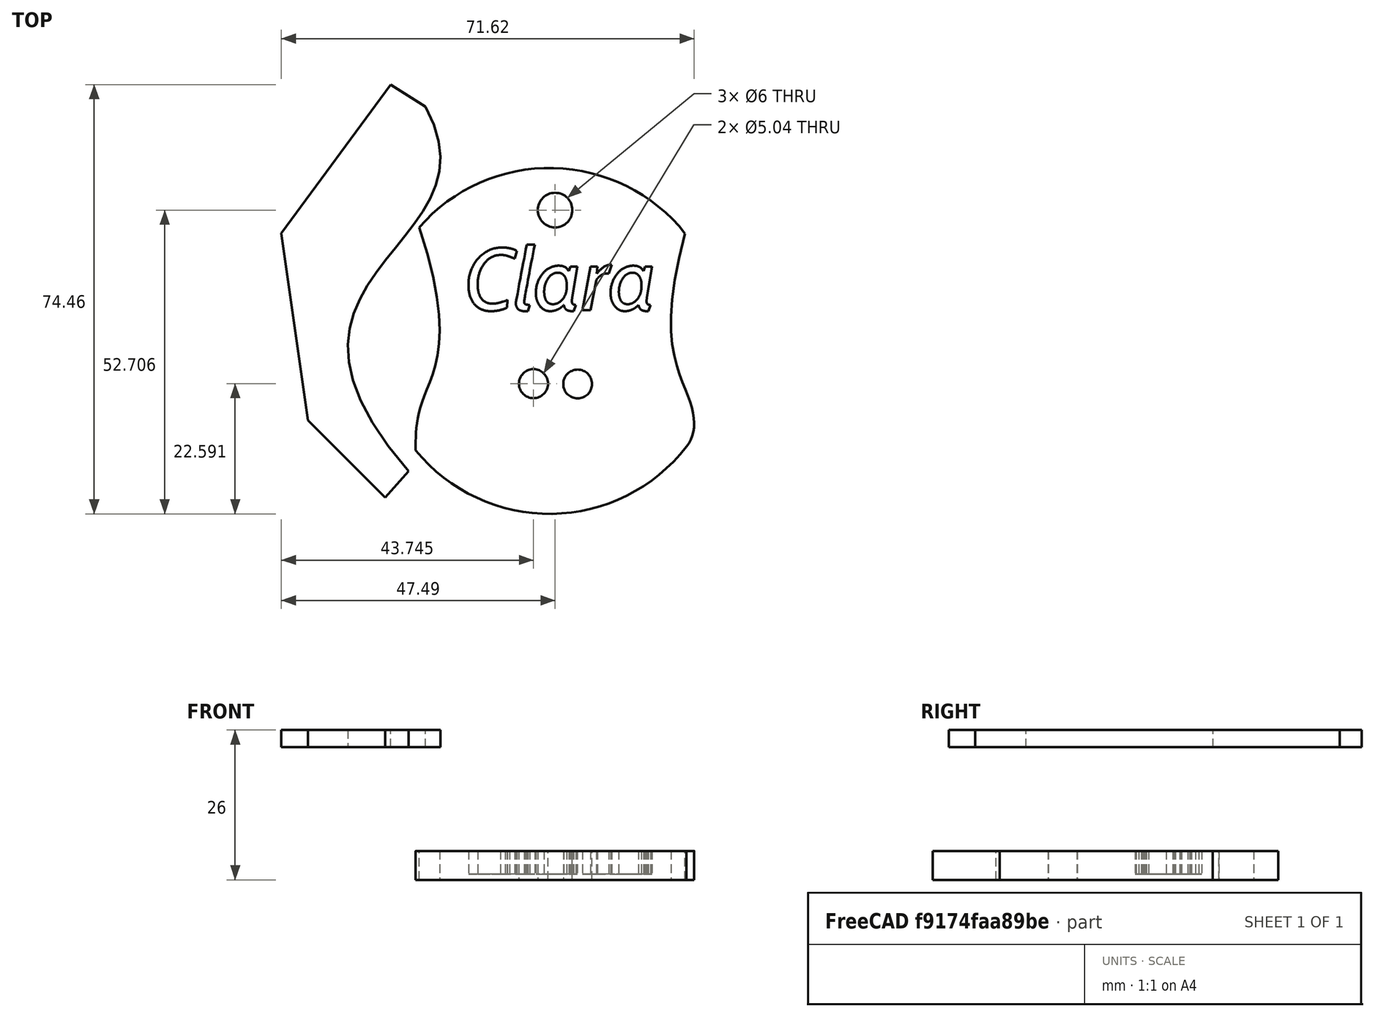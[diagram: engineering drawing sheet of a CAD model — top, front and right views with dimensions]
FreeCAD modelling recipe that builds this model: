
FCSTD DOCUMENT  (FreeCAD 0.17R13541 (Git))
Label: porteClefClaraNum2
License: All rights reserved
LicenseURL: http://en.wikipedia.org/wiki/All_rights_reserved
objects: Part::FeaturePython×2, Part::Extrusion×2, PartDesign::Body×2, Part::Cut×2, Part::Part2DObjectPython×1, Sketcher::SketchObject×1, PartDesign::Pad×1
note: 12 computed .brp shape members not serialized (recipe doc carries the construction recipe); baked Part::Feature solids carry a one-line shape summary decoded from their .brp

FEATURE [Part::FeaturePython] Clone  label="Crane base"  # WARN: FeaturePython — macro-defined, semantics opaque (R4)
  AttacherType = Attacher::AttachEngine3D
  Fuse = false
  Placement = pos=(0,0,2) rot=(0,0,1;0rad)
  Scale = (1,1,1)
FEATURE [Part::FeaturePython] Clone002  label="Crane base001"  # Draft clone (typed FeaturePython)
  AttacherType = Attacher::AttachEngine3D
  Fuse = false
  Objects = -> [Clone]
  Placement = pos=(-16,-38,2) rot=(0,0,1;0rad)
  Scale = (0.08,0.08,1)
FEATURE [Part::Extrusion] Extrude  label="Crane"
  Base = -> Clone002
  Dir = (0,0,1)
  DirMode = 2
  FaceMakerClass = Part::FaceMakerBullseye
  LengthFwd = 3
  LengthRev = 0
  Placement = pos=(-2,8,3) rot=(0,0,1;0rad)
  Solid = true
  Symmetric = false
FEATURE [Part::Part2DObjectPython] ShapeString  label="Clara001"  # Draft 2D object (typed FeaturePython)
  FontFile = <path>
  Placement = pos=(-15.71,-1.64,5) rot=(0,0,1;0rad)
  Size = 6
  String = Clara
  Tracking = 0
FEATURE [Part::Extrusion] Extrude001  label="Clara"
  Base = -> ShapeString
  Dir = (0,0,1)
  DirMode = 2
  FaceMakerClass = Part::FaceMakerBullseye
  LengthFwd = 4
  LengthRev = 0
  Reversed = true
  Solid = true
  Symmetric = false
FEATURE [Sketcher::SketchObject] Sketch001  label="Medaille"
  MapMode = 5
  Support = -> [XY_Plane001]
  sketch-geometry (15):
    g0: Circle CenterX=-0.050083 CenterY=15.7459 CenterZ=0 NormalX=0 NormalY=0 NormalZ=1 AngleXU=0 Radius=3
    g1: Circle CenterX=-3.79519 CenterY=-14.3686 CenterZ=0 NormalX=0 NormalY=0 NormalZ=1 AngleXU=0 Radius=2.51986
    g2: Circle CenterX=3.86768 CenterY=-14.4299 CenterZ=0 NormalX=0 NormalY=0 NormalZ=1 AngleXU=0 Radius=2.49948
    g3-g7: Circle [constr] x5 (B-spline internal-alignment scaffolding for g8; pole/knot coordinates omitted)
    g8: BSplineCurve PolesCount=5 KnotsCount=3 Degree=3 IsPeriodic=0
    g9: GeomPoint [constr] X=-23.6338 Y=12.738 Z=0
    g10: GeomPoint [constr] X=-22.52 Y=-15.8987 Z=0
    g11: GeomPoint [constr] X=-24.2277 Y=-25.9462 Z=0
    g12: ArcOfCircle CenterX=-1.00324 CenterY=-6.95607 CenterZ=0 NormalX=0 NormalY=0 NormalZ=1 AngleXU=0 Radius=30 StartAngle=3.82702 EndAngle=5.62455
    g13: BSplineCurve PolesCount=5 KnotsCount=3 Degree=3 IsPeriodic=0
    g14: ArcOfCircle CenterX=-1.00324 CenterY=-6.95607 CenterZ=0 NormalX=0 NormalY=0 NormalZ=1 AngleXU=0 Radius=30 StartAngle=0.670267 EndAngle=2.42546
  constraints (16):
    c: Radius(g0) = 3
    c: Radius(g3) = 3
    c: Equal(g3, g4-g7) x4
    c: InternalAlignment(g3-g7 -> g8) x5
    c: InternalAlignment(g9,g8)
    c: InternalAlignment(g10,g8)
    c: InternalAlignment(g11,g8)
    c: PointOnObject(g14,g8)
    c: PointOnObject(g12,g8)
    c: Coincident(g12,g7)
    c: Coincident(g3,g14)
    c: Radius(g12) = 30
    c: Equal(g12,g14)
    c: Coincident(g12,g14)
    c: Coincident(g14,g13)
    c: Coincident(g13,g12)
FEATURE [PartDesign::Pad] Pad  label="Base"
  Length = 5
  Length2 = 100
  Profile = -> Sketch001
  Type = 0
FEATURE [PartDesign::Body] Body
  Group = -> [Pad]
  Origin = -> Origin
  Tip = -> Pad
FEATURE [Part::Cut] Cut
  Base = -> Pad
  Tool = -> Extrude
FEATURE [Part::Cut] Cut001
  Base = -> Pad
  Tool = -> Extrude001
FEATURE [PartDesign::Body] Body001  label="cotes"
  Group = -> [Sketch001]
  Origin = -> Origin001
  Placement = pos=(0,0,23) rot=(0,0,1;0rad)
  Tip = -> Body
note: 1 file-system path scrubbed to <path> (originals preserved in the JSON sidecar)
